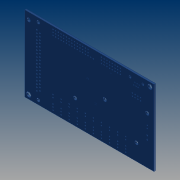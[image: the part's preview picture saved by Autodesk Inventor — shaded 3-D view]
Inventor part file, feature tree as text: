
AUTODESK INVENTOR PART (.ipt)
format: ipt  version: 2012 (Build 160160000, 160)  size: 359,424 bytes
history: native  units: mm (DEFAULTED — no unit token found)
features: plane x3, imported_body x1
ambient origin geometry x5: Origin, X Axis, Y Axis, Z Axis, Center Point
bodies: Solid1 (feature_tree)
feature tree (4):
  imported_body  "Base1"
  plane  "YZ Plane (RIGHT)"
  plane  "XZ Plane (TOP)"
  plane  "XY Plane (FRONT)"
